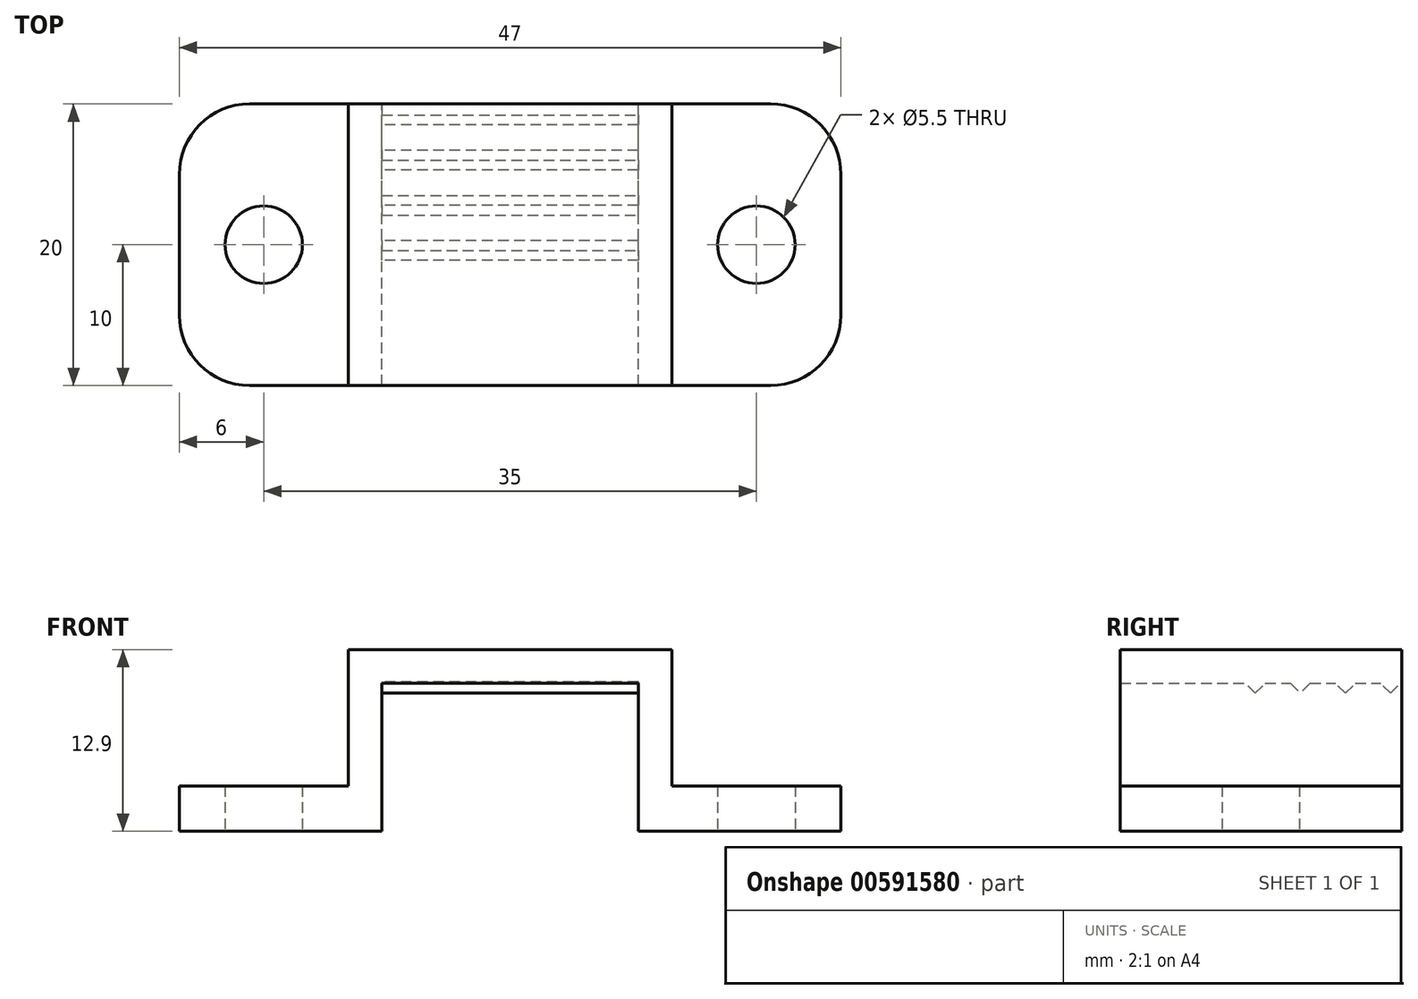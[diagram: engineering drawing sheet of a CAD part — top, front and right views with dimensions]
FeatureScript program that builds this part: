
annotation { "Feature Type Name" : "Feature", "Feature Type Description" : "" }
export const myFeature = defineFeature(function(context is Context, id is Id, definition is map)
    precondition{}
    {
        {
            var Q0;
            Q0=qCreatedBy(makeId("Front.planeOp"),FACE);
            var sketch = newSketch(context, id + "F0", { "sketchPlane" : qUnion([Q0])});
            skLineSegment(sketch, "E0.bottom", {"start": v(0, 10.5) * mm, "end": v(-9.1, 10.5) * mm});
            skLineSegment(sketch, "E0.top", {"start": v(0, 0) * mm, "end": v(-9.1, 0) * mm});
            skLineSegment(sketch, "E0.left", {"start": v(0, 10.5) * mm, "end": v(0, 0) * mm});
            skLineSegment(sketch, "E0.right", {"start": v(-9.1, 10.5) * mm, "end": v(-9.1, 0) * mm});
            skLineSegment(sketch, "E1.bottom", {"start": v(0, 0) * mm, "end": v(-11.5, 0) * mm});
            skLineSegment(sketch, "E1.top", {"start": v(0, 12.9) * mm, "end": v(-11.5, 12.9) * mm});
            skLineSegment(sketch, "E1.left", {"start": v(0, 0) * mm, "end": v(0, 12.9) * mm});
            skLineSegment(sketch, "E1.right", {"start": v(-11.5, 0) * mm, "end": v(-11.5, 12.9) * mm});
            skLineSegment(sketch, "E2.bottom", {"start": v(-11.5, 0) * mm, "end": v(-23.5, 0) * mm});
            skLineSegment(sketch, "E2.top", {"start": v(-11.5, 3.2) * mm, "end": v(-23.5, 3.2) * mm});
            skLineSegment(sketch, "E2.left", {"start": v(-11.5, 0) * mm, "end": v(-11.5, 3.2) * mm});
            skLineSegment(sketch, "E2.right", {"start": v(-23.5, 0) * mm, "end": v(-23.5, 3.2) * mm});
            skLineSegment(sketch, "E3.MirrorCS", {"start": v(0, 10.5) * mm, "end": v(9.1, 10.5) * mm});
            skLineSegment(sketch, "E4.MirrorCS", {"start": v(9.1, 10.5) * mm, "end": v(9.1, 0) * mm});
            skLineSegment(sketch, "E5.MirrorCS", {"start": v(11.5, 0) * mm, "end": v(11.5, 12.9) * mm});
            skLineSegment(sketch, "E6.MirrorCS", {"start": v(0, 12.9) * mm, "end": v(11.5, 12.9) * mm});
            skLineSegment(sketch, "E7.MirrorCS", {"start": v(11.5, 3.2) * mm, "end": v(23.5, 3.2) * mm});
            skLineSegment(sketch, "E8.MirrorCS", {"start": v(23.5, 0) * mm, "end": v(23.5, 3.2) * mm});
            skLineSegment(sketch, "E9.MirrorCS", {"start": v(11.5, 0) * mm, "end": v(23.5, 0) * mm});
            skLineSegment(sketch, "E10.MirrorCS", {"start": v(0, 0) * mm, "end": v(11.5, 0) * mm});
            skSolve(sketch);
        }
        {
            var Q0;
            {var subQ4=sQuery(id+"F0.wireOp",EDGE,"E0.bottom");Q0=makeQuery(id+"F0.imprint","IMPRINT",FACE,{"disambiguationData":[TD([[makeQuery(id+"F0.imprint","IMPRINT",EDGE,{"derivedFrom":subQ4}),-1.0]])]});}
            var Q1;
            Q1=makeQuery(id+"F0.imprint","IMPRINT",FACE,{"disambiguationData":[TD([[makeQuery(id+"F0.imprint","IMPRINT",EDGE,{"derivedFrom":sQuery(id+"F0.wireOp",EDGE,"E2.bottom")}),-1.0]])]});
            var Q2;
            {var subQ5=sQuery(id+"F0.wireOp",EDGE,"E3.MirrorCS");Q2=makeQuery(id+"F0.imprint","IMPRINT",FACE,{"disambiguationData":[TD([[makeQuery(id+"F0.imprint","IMPRINT",EDGE,{"derivedFrom":subQ5}),1.0]])]});}
            var Q3;
            {var subQ2=sQuery(id+"F0.wireOp",EDGE,"E7.MirrorCS");Q3=makeQuery(id+"F0.imprint","IMPRINT",FACE,{"disambiguationData":[TD([[makeQuery(id+"F0.imprint","IMPRINT",EDGE,{"derivedFrom":subQ2}),-1.0]])]});}
            extrude(context, id + "F1", {"entities" : qUnion([Q0, Q1, Q2, Q3]), "depth" : 20 * mm, "offsetDistance" : 25 * mm});
        }
        {
            var Q0;
            Q0=makeQuery(id+"F1.opExtrude","SWEPT_FACE",FACE,{"disambiguationData":[OSD([sQuery(id+"F0.wireOp",EDGE,"E2.top")])]});
            var sketch = newSketch(context, id + "F2", { "sketchPlane" : qUnion([Q0])});
            skPoint(sketch, "E11", {"position": v(-17.5, -10) * mm});
            skPoint(sketch, "E11.positionSnap0", {"position": v(-17.5, 0) * mm});
            skPoint(sketch, "E11.positionSnap1", {"position": v(-23.5, -10) * mm});
            skPoint(sketch, "E12.MirrorP", {"position": v(17.5, -10) * mm});
            skSolve(sketch);
        }
        {
            var Q0;
            Q0=sQuery(id+"F2.wireOp",VERTEX,"E11");
            var Q1;
            Q1=sQuery(id+"F2.wireOp",VERTEX,"E12.MirrorP");
            var Q2;
            Q2=makeQuery(id+"F1.opExtrude","SWEPT_BODY",BODY,{"disambiguationData":[OSD([sQuery(id+"F0.wireOp",EDGE,"E0.bottom"),sQuery(id+"F0.wireOp",EDGE,"E0.right"),sQuery(id+"F0.wireOp",EDGE,"E1.bottom"),sQuery(id+"F0.wireOp",EDGE,"E1.top"),sQuery(id+"F0.wireOp",EDGE,"E1.right"),sQuery(id+"F0.wireOp",EDGE,"E2.bottom"),sQuery(id+"F0.wireOp",EDGE,"E2.top"),sQuery(id+"F0.wireOp",EDGE,"E2.right"),sQuery(id+"F0.wireOp",EDGE,"E3.MirrorCS"),sQuery(id+"F0.wireOp",EDGE,"E4.MirrorCS"),sQuery(id+"F0.wireOp",EDGE,"E5.MirrorCS"),sQuery(id+"F0.wireOp",EDGE,"E6.MirrorCS"),sQuery(id+"F0.wireOp",EDGE,"E7.MirrorCS"),sQuery(id+"F0.wireOp",EDGE,"E8.MirrorCS"),sQuery(id+"F0.wireOp",EDGE,"E9.MirrorCS"),sQuery(id+"F0.wireOp",EDGE,"E10.MirrorCS")])]});
            hole(context, id + "F3", {"style" : HoleStyle.SIMPLE, "endStyle" : HoleEndStyle.THROUGH, "standardTappedOrClearance" : lookupTablePath({ "standard" : "ISO", "fit" : "Normal", "size" : "M5", "type" : "Clearance" }), "standardBlindInLast" : lookupTablePath({ "fit" : "Standard", "standard" : "ISO", "size" : "M5", "type" : "Clearance" }), "holeDiameter" : 5.5 * mm, "majorDiameter" : 5 * mm, "isTappedThrough" : true, "tappedDepth" : 12 * mm, "tapClearance" : 3, "locations" : qUnion([Q0, Q1]), "scope" : qUnion([Q2])});
        }
        {
            var Q0;
            Q0=makeQuery(id+"F1.opExtrude","SWEPT_FACE",FACE,{"disambiguationData":[OSD([sQuery(id+"F0.wireOp",EDGE,"E0.bottom"),sQuery(id+"F0.wireOp",EDGE,"E3.MirrorCS")])]});
            var sketch = newSketch(context, id + "F4", { "sketchPlane" : qUnion([Q0])});
            skLineSegment(sketch, "E13.bottom", {"start": v(-9.1, 0) * mm, "end": v(9.1, 0) * mm});
            skLineSegment(sketch, "E13.top", {"start": v(-9.1, 1.6) * mm, "end": v(9.1, 1.6) * mm});
            skLineSegment(sketch, "E13.left", {"start": v(-9.1, 0) * mm, "end": v(-9.1, 1.6) * mm});
            skLineSegment(sketch, "E13.right", {"start": v(9.1, 0) * mm, "end": v(9.1, 1.6) * mm});
            skLineSegment(sketch, "E14.bottom", {"start": v(-9.1, 3.2) * mm, "end": v(9.1, 3.2) * mm});
            skLineSegment(sketch, "E14.top", {"start": v(-9.1, 4.8) * mm, "end": v(9.1, 4.8) * mm});
            skLineSegment(sketch, "E14.left", {"start": v(-9.1, 3.2) * mm, "end": v(-9.1, 4.8) * mm});
            skLineSegment(sketch, "E14.right", {"start": v(9.1, 3.2) * mm, "end": v(9.1, 4.8) * mm});
            skLineSegment(sketch, "E15.bottom", {"start": v(9.1, 6.4) * mm, "end": v(-9.1, 6.4) * mm});
            skLineSegment(sketch, "E15.top", {"start": v(9.1, 8) * mm, "end": v(-9.1, 8) * mm});
            skLineSegment(sketch, "E15.left", {"start": v(9.1, 6.4) * mm, "end": v(9.1, 8) * mm});
            skLineSegment(sketch, "E15.right", {"start": v(-9.1, 6.4) * mm, "end": v(-9.1, 8) * mm});
            skLineSegment(sketch, "E16.bottom", {"start": v(-9.1, 9.6) * mm, "end": v(9.1, 9.6) * mm});
            skLineSegment(sketch, "E16.top", {"start": v(-9.1, 11.2) * mm, "end": v(9.1, 11.2) * mm});
            skLineSegment(sketch, "E16.left", {"start": v(-9.1, 9.6) * mm, "end": v(-9.1, 11.2) * mm});
            skLineSegment(sketch, "E16.right", {"start": v(9.1, 9.6) * mm, "end": v(9.1, 11.2) * mm});
            skSolve(sketch);
        }
        {
            var Q0;
            Q0=makeQuery(id+"F4.imprint","IMPRINT",FACE,{"disambiguationData":[TD([[makeQuery(id+"F4.imprint","IMPRINT",EDGE,{"derivedFrom":sQuery(id+"F4.wireOp",EDGE,"E13.bottom")}),-1.0]])]});
            var Q1;
            Q1=makeQuery(id+"F4.imprint","IMPRINT",FACE,{"disambiguationData":[TD([[makeQuery(id+"F4.imprint","IMPRINT",EDGE,{"derivedFrom":sQuery(id+"F4.wireOp",EDGE,"E14.bottom")}),1.0]])]});
            var Q2;
            Q2=makeQuery(id+"F4.imprint","IMPRINT",FACE,{"disambiguationData":[TD([[makeQuery(id+"F4.imprint","IMPRINT",EDGE,{"derivedFrom":sQuery(id+"F4.wireOp",EDGE,"E15.bottom")}),-1.0]])]});
            var Q3;
            Q3=makeQuery(id+"F4.imprint","IMPRINT",FACE,{"disambiguationData":[TD([[makeQuery(id+"F4.imprint","IMPRINT",EDGE,{"derivedFrom":sQuery(id+"F4.wireOp",EDGE,"E16.bottom")}),1.0]])]});
            extrude(context, id + "F5", {"entities" : qUnion([Q0, Q1, Q2, Q3]), "operationType" : NewBodyOperationType.ADD, "depth" : .9 * mm, "offsetDistance" : 25 * mm});
        }
        {
            var Q0;
            Q0=makeQuery(id+"F5.opExtrude","CAP_EDGE",EDGE,{"disambiguationData":[OSD([sQuery(id+"F4.wireOp",EDGE,"E13.top")])],"isStart":false});
            var Q1;
            Q1=makeQuery(id+"F5.opExtrude","CAP_EDGE",EDGE,{"disambiguationData":[OSD([sQuery(id+"F4.wireOp",EDGE,"E13.bottom")])],"isStart":false});
            var Q2;
            Q2=makeQuery(id+"F5.opExtrude","CAP_EDGE",EDGE,{"disambiguationData":[OSD([sQuery(id+"F4.wireOp",EDGE,"E14.bottom")])],"isStart":false});
            var Q3;
            Q3=makeQuery(id+"F5.opExtrude","CAP_EDGE",EDGE,{"disambiguationData":[OSD([sQuery(id+"F4.wireOp",EDGE,"E14.top")])],"isStart":false});
            var Q4;
            Q4=makeQuery(id+"F5.opExtrude","CAP_EDGE",EDGE,{"disambiguationData":[OSD([sQuery(id+"F4.wireOp",EDGE,"E15.bottom")])],"isStart":false});
            var Q5;
            Q5=makeQuery(id+"F5.opExtrude","CAP_EDGE",EDGE,{"disambiguationData":[OSD([sQuery(id+"F4.wireOp",EDGE,"E15.top")])],"isStart":false});
            var Q6;
            Q6=makeQuery(id+"F5.opExtrude","CAP_EDGE",EDGE,{"disambiguationData":[OSD([sQuery(id+"F4.wireOp",EDGE,"E16.bottom")])],"isStart":false});
            var Q7;
            Q7=makeQuery(id+"F5.opExtrude","CAP_EDGE",EDGE,{"disambiguationData":[OSD([sQuery(id+"F4.wireOp",EDGE,"E16.top")])],"isStart":false});
            chamfer(context, id + "F6", {"entities" : qUnion([Q0, Q1, Q2, Q3, Q4, Q5, Q6, Q7]), "width" : 1 * mm, "tangentPropagation" : true});
        }
        {
            var Q0;
            Q0=makeQuery(id+"F1.opExtrude","CAP_EDGE",EDGE,{"disambiguationData":[OSD([sQuery(id+"F0.wireOp",EDGE,"E2.right")])],"isStart":false});
            var Q1;
            Q1=makeQuery(id+"F1.opExtrude","CAP_EDGE",EDGE,{"disambiguationData":[OSD([sQuery(id+"F0.wireOp",EDGE,"E8.MirrorCS")])],"isStart":false});
            var Q2;
            Q2=makeQuery(id+"F1.opExtrude","CAP_EDGE",EDGE,{"disambiguationData":[OSD([sQuery(id+"F0.wireOp",EDGE,"E8.MirrorCS")])],"isStart":true});
            var Q3;
            Q3=makeQuery(id+"F1.opExtrude","CAP_EDGE",EDGE,{"disambiguationData":[OSD([sQuery(id+"F0.wireOp",EDGE,"E2.right")])],"isStart":true});
            fillet(context, id + "F7", {"entities" : qUnion([Q0, Q1, Q2, Q3]), "radius" : 5 * mm, "tangentPropagation" : true, "allowEdgeOverflow" : false});
        }
    });
